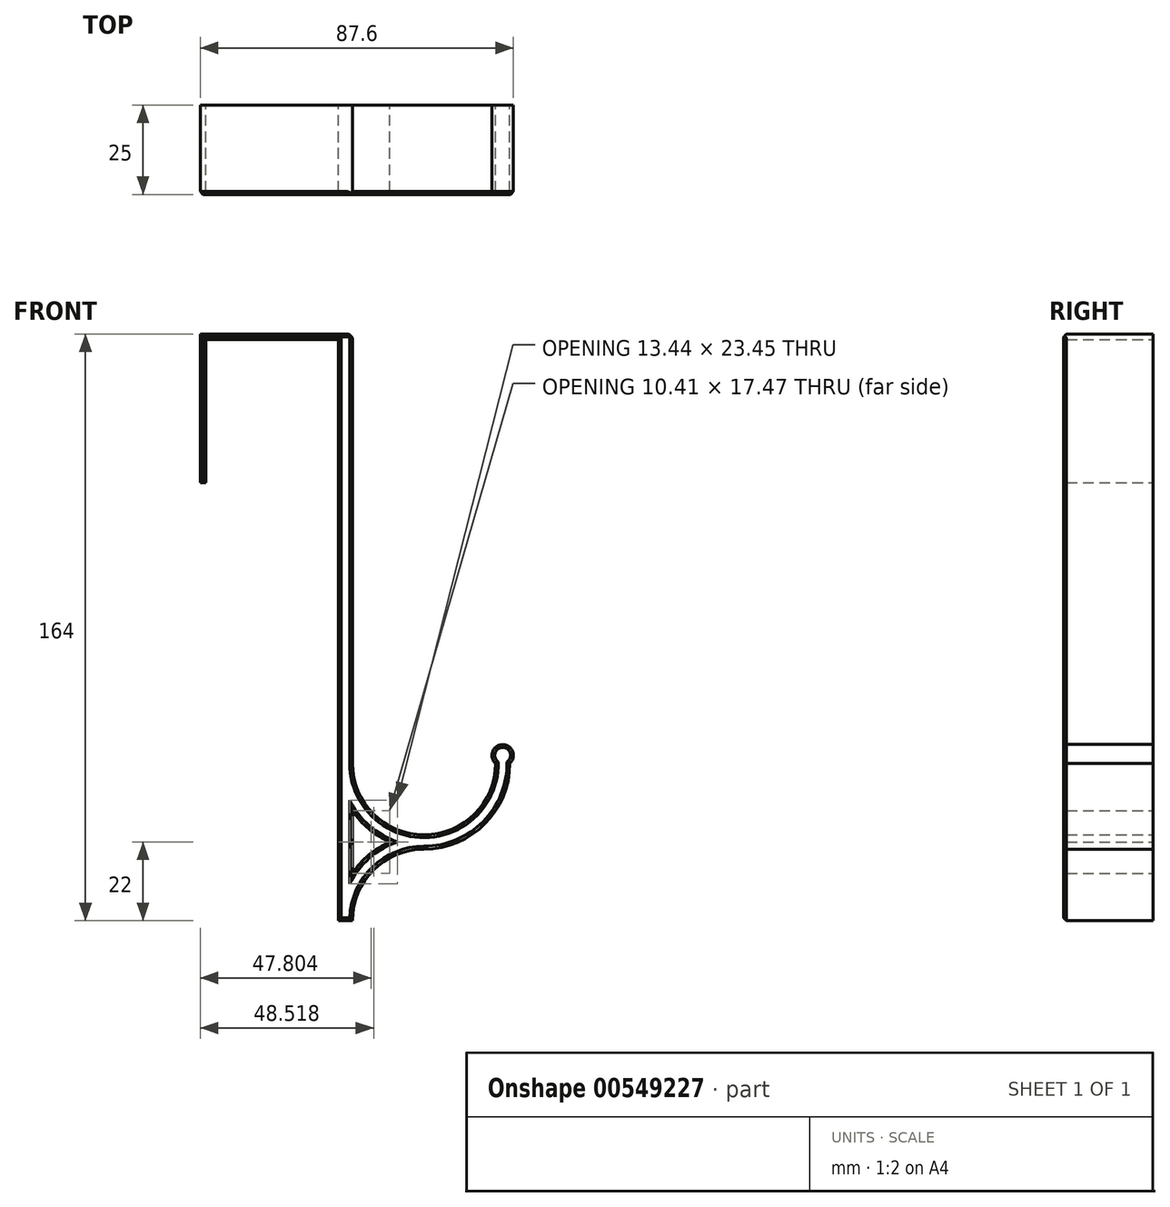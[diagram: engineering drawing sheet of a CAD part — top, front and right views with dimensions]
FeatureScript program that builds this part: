
annotation { "Feature Type Name" : "Feature", "Feature Type Description" : "" }
export const myFeature = defineFeature(function(context is Context, id is Id, definition is map)
    precondition{}
    {
        {
            var Q0;
            Q0=qCreatedBy(makeId("Front.planeOp"),FACE);
            var sketch = newSketch(context, id + "F0", { "sketchPlane" : qUnion([Q0])});
            skLineSegment(sketch, "E0", {"start": v(0, 0) * mm, "end": v(1.6, 0) * mm});
            skLineSegment(sketch, "E1", {"start": v(1.6, 0) * mm, "end": v(1.6, 40) * mm});
            skLineSegment(sketch, "E2", {"start": v(1.6, 40) * mm, "end": v(38.6, 40) * mm});
            skLineSegment(sketch, "E3", {"start": v(38.6, 40) * mm, "end": v(38.6, -78.4) * mm});
            skLineSegment(sketch, "E4", {"start": v(42.6, -78.4) * mm, "end": v(42.6, 41.6) * mm});
            skLineSegment(sketch, "E5", {"start": v(42.6, 41.6) * mm, "end": v(0, 41.6) * mm});
            skLineSegment(sketch, "E6", {"start": v(0, 41.6) * mm, "end": v(0, 0) * mm});
            skArc(sketch, "E7", {"start": v(42.6, -78.4) * mm, "mid": v(62.6, -98.4) * mm, "end": v(82.6, -78.4) * mm});
            skArc(sketch, "E8", {"start": v(42.6, -91.67) * mm, "mid": v(47.17, -96.79) * mm, "end": v(53, -100.4) * mm});
            skLineSegment(sketch, "E9", {"start": v(82.6, -78.4) * mm, "end": v(86.6, -78.4) * mm, "construction": true});
            skArc(sketch, "E10", {"start": v(86.6, -78.4) * mm, "mid": v(84.6, -73.16) * mm, "end": v(82.6, -78.4) * mm});
            skPoint(sketch, "E10.third.point", {"position": v(84.6, -73.16) * mm});
            skPoint(sketch, "E10.third.point.positionSnap0", {"position": v(84.6, -78.4) * mm});
            skLineSegment(sketch, "E11", {"start": v(38.6, -78.4) * mm, "end": v(38.6, -122.4) * mm});
            skLineSegment(sketch, "E12", {"start": v(38.6, -122.4) * mm, "end": v(42.6, -122.4) * mm});
            skLineSegment(sketch, "E13", {"start": v(42.6, -109.13) * mm, "end": v(42.6, -91.67) * mm});
            skArc(sketch, "E14", {"start": v(53, -100.4) * mm, "mid": v(47.17, -104.01) * mm, "end": v(42.6, -109.13) * mm});
            skArc(sketch, "E15", {"start": v(62.6, -102.4) * mm, "mid": v(48.46, -108.26) * mm, "end": v(42.6, -122.4) * mm});
            skArc(sketch, "E16.trimOffspring", {"start": v(62.6, -102.4) * mm, "mid": v(79.57, -95.37) * mm, "end": v(86.6, -78.4) * mm});
            skSolve(sketch);
        }
        {
            var Q0;
            Q0 = qSketchRegion(id + "F0", true);
            extrude(context, id + "F1", {"entities" : qUnion([Q0]), "depth" : 25 * mm, "offsetDistance" : 25 * mm});
        }
        {
            var Q0;
            Q0=makeQuery(id+"F1.opExtrude","CAP_FACE",FACE,{"disambiguationData":[OSD([sQuery(id+"F0.wireOp",EDGE,"E0"),sQuery(id+"F0.wireOp",EDGE,"E1"),sQuery(id+"F0.wireOp",EDGE,"E2"),sQuery(id+"F0.wireOp",EDGE,"E3"),sQuery(id+"F0.wireOp",EDGE,"E4"),sQuery(id+"F0.wireOp",EDGE,"E5"),sQuery(id+"F0.wireOp",EDGE,"E6"),sQuery(id+"F0.wireOp",EDGE,"E7"),sQuery(id+"F0.wireOp",EDGE,"E8"),sQuery(id+"F0.wireOp",EDGE,"E10")])],"isStart":false});
            chamfer(context, id + "F2", {"entities" : qUnion([Q0]), "width" : 0.8 * mm, "tangentPropagation" : true});
        }
        {
            var Q0;
            Q0=makeQuery(id+"F1.opExtrude","SWEPT_EDGE",EDGE,{"disambiguationData":[OSD([sQuery(id+"F0.wireOp",EDGE,"E4"),sQuery(id+"F0.wireOp",EDGE,"E5")])]});
            fillet(context, id + "F3", {"entities" : qUnion([Q0]), "radius" : 1.6 * mm, "tangentPropagation" : true, "allowEdgeOverflow" : false});
        }
    });
